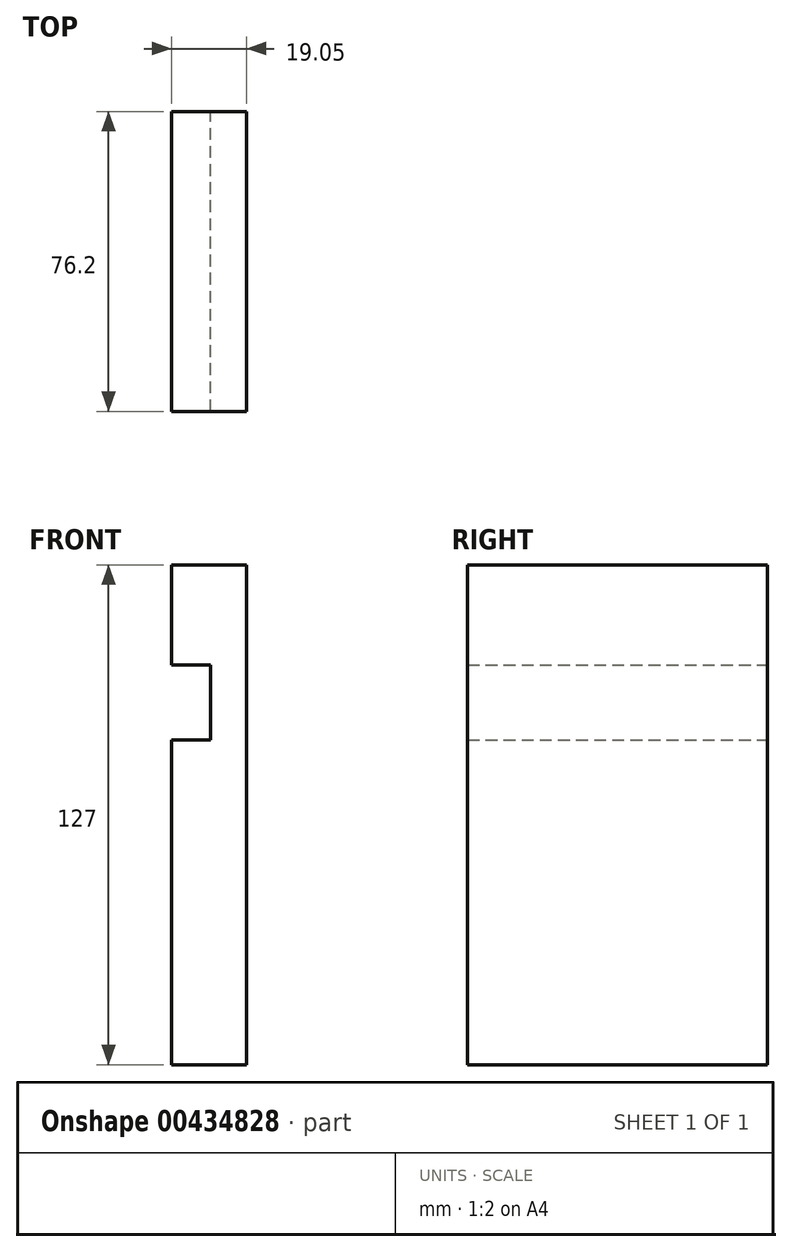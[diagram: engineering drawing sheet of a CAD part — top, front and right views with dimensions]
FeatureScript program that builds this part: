
annotation { "Feature Type Name" : "Feature", "Feature Type Description" : "" }
export const myFeature = defineFeature(function(context is Context, id is Id, definition is map)
    precondition{}
    {
        {
            var Q0;
            Q0=qCreatedBy(makeId("Front.planeOp"),FACE);
            var sketch = newSketch(context, id + "F0", { "sketchPlane" : qUnion([Q0])});
            skLineSegment(sketch, "E0", {"start": v(10.31, -62.63) * mm, "end": v(29.36, -62.63) * mm});
            skLineSegment(sketch, "E1", {"start": v(29.36, -62.63) * mm, "end": v(29.36, 64.37) * mm});
            skLineSegment(sketch, "E2", {"start": v(29.36, 64.37) * mm, "end": v(10.31, 64.37) * mm});
            skLineSegment(sketch, "E3", {"start": v(10.31, 64.37) * mm, "end": v(10.31, 38.97) * mm});
            skLineSegment(sketch, "E4", {"start": v(10.31, 38.97) * mm, "end": v(20.24, 38.97) * mm});
            skLineSegment(sketch, "E5", {"start": v(20.24, 38.97) * mm, "end": v(20.24, 19.92) * mm});
            skLineSegment(sketch, "E6", {"start": v(20.24, 19.92) * mm, "end": v(10.31, 19.92) * mm});
            skLineSegment(sketch, "E7", {"start": v(10.31, 19.92) * mm, "end": v(10.31, -62.63) * mm});
            skSolve(sketch);
        }
        {
            var Q0;
            Q0 = qSketchRegion(id + "F0", true);
            extrude(context, id + "F1", {"entities" : qUnion([Q0]), "depth" : 76.2 * mm});
        }
    });
